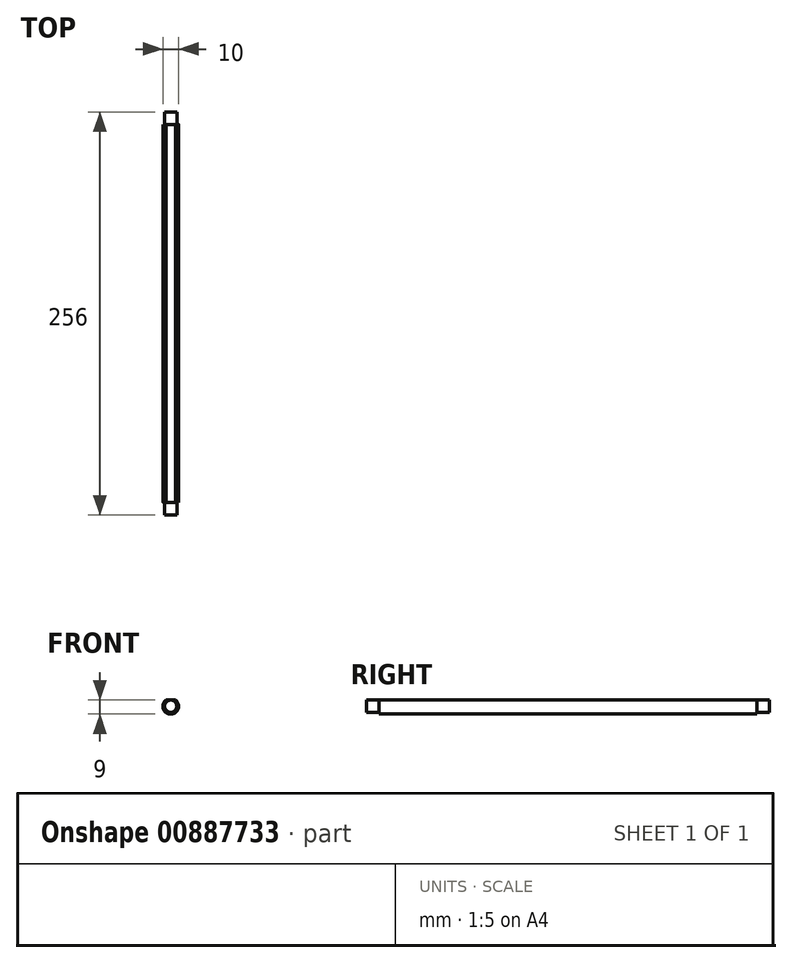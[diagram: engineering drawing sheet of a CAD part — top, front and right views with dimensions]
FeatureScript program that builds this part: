
annotation { "Feature Type Name" : "Feature", "Feature Type Description" : "" }
export const myFeature = defineFeature(function(context is Context, id is Id, definition is map)
    precondition{}
    {
        {
            var Q0;
            Q0=qCreatedBy(makeId("Front.planeOp"),FACE);
            var sketch = newSketch(context, id + "F0", { "sketchPlane" : qUnion([Q0])});
            skArc(sketch, "E0", {"start": v(-3, 4) * mm, "mid": v(0, -5) * mm, "end": v(3, 4) * mm});
            skLineSegment(sketch, "E1", {"start": v(-3, 4) * mm, "end": v(3, 4) * mm});
            skPoint(sketch, "E2.orphan", {"position": v(10.73, 4) * mm});
            skSolve(sketch);
        }
        {
            var Q0;
            Q0 = qSketchRegion(id + "F0", true);
            extrude(context, id + "F1", {"entities" : qUnion([Q0]), "endBound" : BoundingType.SYMMETRIC, "depth" : 240 * mm, "offsetDistance" : 25 * mm});
        }
        {
            var Q0;
            Q0=makeQuery(id+"F1.opExtrude","CAP_FACE",FACE,{"disambiguationData":[OSD([sQuery(id+"F0.wireOp",EDGE,"E0"),sQuery(id+"F0.wireOp",EDGE,"E1")])],"isStart":false});
            var sketch = newSketch(context, id + "F2", { "sketchPlane" : qUnion([Q0])});
            skCircle(sketch, "E3", {"center": v(0, 0) * mm, "radius": 3.88 * mm});
            skSolve(sketch);
        }
        {
            var Q0;
            Q0=makeQuery(id+"F1.opExtrude","CAP_FACE",FACE,{"disambiguationData":[OSD([sQuery(id+"F0.wireOp",EDGE,"E0"),sQuery(id+"F0.wireOp",EDGE,"E1")])],"isStart":true});
            var sketch = newSketch(context, id + "F3", { "sketchPlane" : qUnion([Q0])});
            skCircle(sketch, "E4", {"center": v(0, 0) * mm, "radius": 3.88 * mm});
            skSolve(sketch);
        }
        {
            var Q0;
            Q0=makeQuery(id+"F3.imprint","IMPRINT",FACE,{"disambiguationData":[TD([[makeQuery(id+"F3.imprint","IMPRINT",EDGE,{"derivedFrom":sQuery(id+"F3.wireOp",EDGE,"E4")}),1.0]])]});
            extrude(context, id + "F4", {"entities" : qUnion([Q0]), "operationType" : NewBodyOperationType.ADD, "depth" : 8 * mm, "offsetDistance" : 25 * mm});
        }
        {
            var Q0;
            Q0=makeQuery(id+"F2.imprint","IMPRINT",FACE,{"disambiguationData":[TD([[makeQuery(id+"F2.imprint","IMPRINT",EDGE,{"derivedFrom":sQuery(id+"F2.wireOp",EDGE,"E3")}),1.0]])]});
            extrude(context, id + "F5", {"entities" : qUnion([Q0]), "operationType" : NewBodyOperationType.ADD, "depth" : 8 * mm, "offsetDistance" : 25 * mm});
        }
    });
